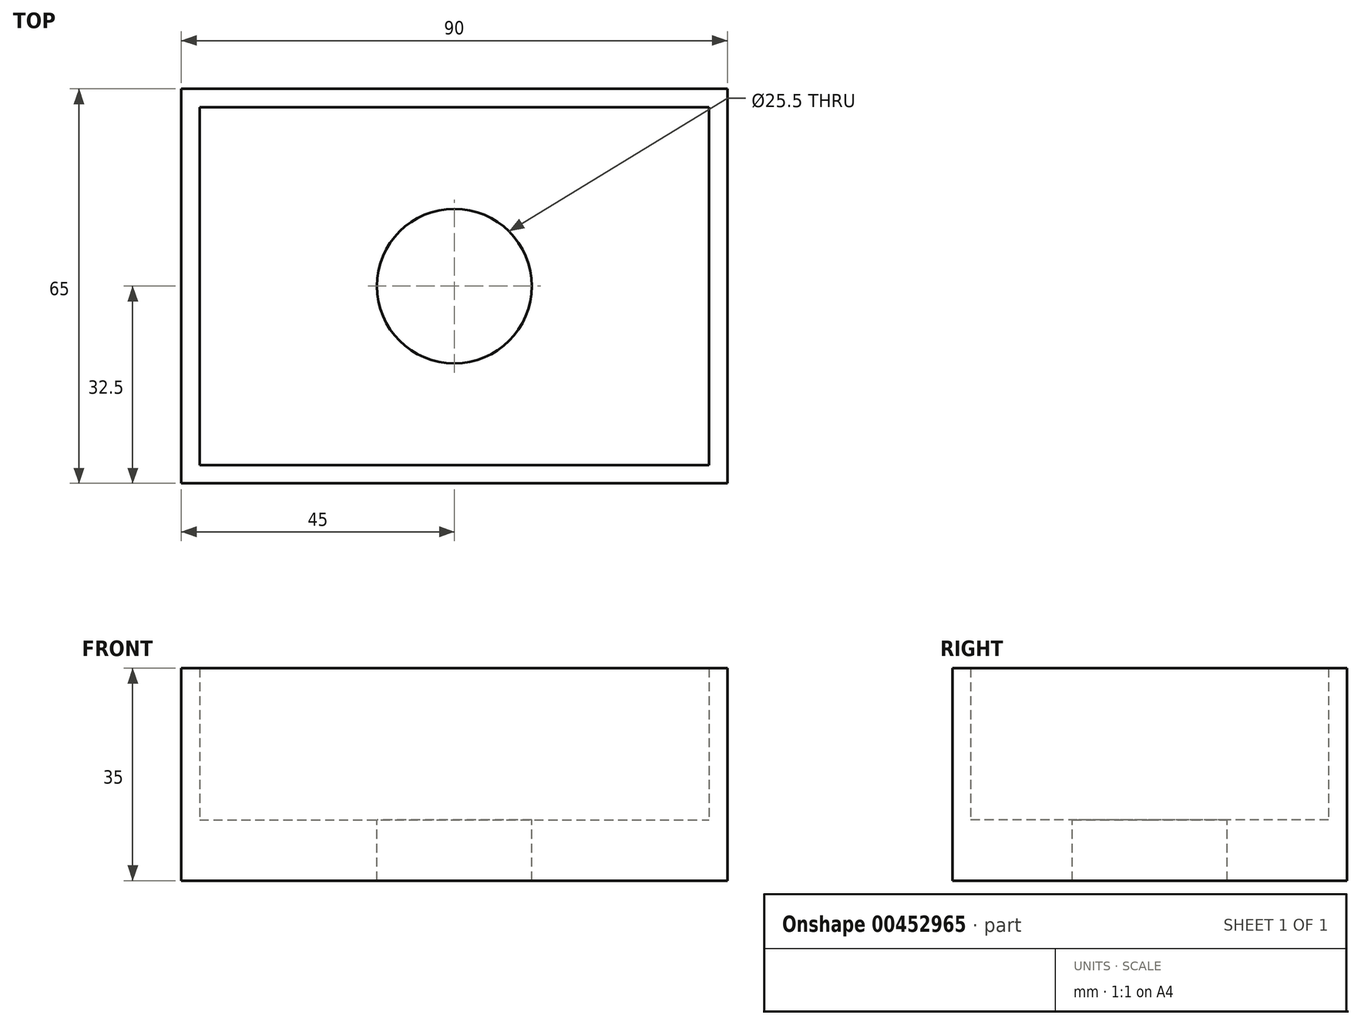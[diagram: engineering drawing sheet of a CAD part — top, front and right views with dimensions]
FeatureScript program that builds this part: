
annotation { "Feature Type Name" : "Feature", "Feature Type Description" : "" }
export const myFeature = defineFeature(function(context is Context, id is Id, definition is map)
    precondition{}
    {
        {
            var Q0;
            Q0=qCreatedBy(makeId("Top.planeOp"),FACE);
            var sketch = newSketch(context, id + "F0", { "sketchPlane" : qUnion([Q0])});
            skLineSegment(sketch, "E0.bottom", {"start": v(-45, 32.5) * mm, "end": v(45, 32.5) * mm});
            skLineSegment(sketch, "E0.top", {"start": v(-45, -32.5) * mm, "end": v(45, -32.5) * mm});
            skLineSegment(sketch, "E0.left", {"start": v(-45, 32.5) * mm, "end": v(-45, -32.5) * mm});
            skLineSegment(sketch, "E0.right", {"start": v(45, 32.5) * mm, "end": v(45, -32.5) * mm});
            skSolve(sketch);
        }
        {
            var Q0;
            Q0 = qSketchRegion(id + "F0", true);
            extrude(context, id + "F1", {"entities" : qUnion([Q0]), "depth" : 10 * mm});
        }
        {
            var Q0;
            Q0=makeQuery(id+"F1.opExtrude","CAP_FACE",FACE,{"disambiguationData":[OSD([sQuery(id+"F0.wireOp",EDGE,"E0.bottom"),sQuery(id+"F0.wireOp",EDGE,"E0.top"),sQuery(id+"F0.wireOp",EDGE,"E0.left"),sQuery(id+"F0.wireOp",EDGE,"E0.right")])],"isStart":false});
            var sketch = newSketch(context, id + "F2", { "sketchPlane" : qUnion([Q0])});
            skCircle(sketch, "E1", {"center": v(0, 0) * mm, "radius": 12.75 * mm});
            skSolve(sketch);
        }
        {
            var Q0;
            Q0 = qSketchRegion(id + "F2", true);
            extrude(context, id + "F3", {"entities" : qUnion([Q0]), "operationType" : NewBodyOperationType.REMOVE, "oppositeDirection" : true, "depth" : 10 * mm});
        }
        {
            var Q0;
            Q0=makeQuery(id+"F1.opExtrude","CAP_FACE",FACE,{"disambiguationData":[OSD([sQuery(id+"F0.wireOp",EDGE,"E0.bottom"),sQuery(id+"F0.wireOp",EDGE,"E0.top"),sQuery(id+"F0.wireOp",EDGE,"E0.left"),sQuery(id+"F0.wireOp",EDGE,"E0.right")])],"isStart":false});
            var sketch = newSketch(context, id + "F4", { "sketchPlane" : qUnion([Q0])});
            skLineSegment(sketch, "E2.bottom", {"start": v(-45, 32.5) * mm, "end": v(45, 32.5) * mm});
            skLineSegment(sketch, "E2.top", {"start": v(-45, -32.5) * mm, "end": v(45, -32.5) * mm});
            skLineSegment(sketch, "E2.left", {"start": v(-45, 32.5) * mm, "end": v(-45, -32.5) * mm});
            skLineSegment(sketch, "E2.right", {"start": v(45, 32.5) * mm, "end": v(45, -32.5) * mm});
            skLineSegment(sketch, "E3.bottom", {"start": v(-42, 29.5) * mm, "end": v(42, 29.5) * mm});
            skLineSegment(sketch, "E3.top", {"start": v(-42, -29.5) * mm, "end": v(42, -29.5) * mm});
            skLineSegment(sketch, "E3.left", {"start": v(-42, 29.5) * mm, "end": v(-42, -29.5) * mm});
            skLineSegment(sketch, "E3.right", {"start": v(42, 29.5) * mm, "end": v(42, -29.5) * mm});
            skSolve(sketch);
        }
        {
            var Q0;
            Q0 = qSketchRegion(id + "F4", true);
            extrude(context, id + "F5", {"entities" : qUnion([Q0]), "operationType" : NewBodyOperationType.ADD, "depth" : 25 * mm});
        }
    });
